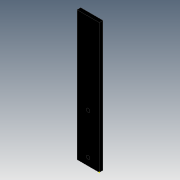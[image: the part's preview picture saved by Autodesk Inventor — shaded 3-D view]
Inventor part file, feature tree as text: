
AUTODESK INVENTOR PART (.ipt)
format: ipt  version: 2015 (Build 190159000, 159)  size: 95,232 bytes
history: native  units: mm
features: other x4, sketch x2, extrude x1, projected_geometry x1
ambient origin geometry x8: Origin, YZ Plane, XZ Plane, XY Plane, X Axis, Y Axis, Z Axis, Center Point
bodies: Body1 (feature_tree)
feature tree (8):
  other  "Blocks"
  extrude  "Extrusion3"  Depth=150.0mm
  sketch  "Sketch3"  dims[d0=60.0mm d1=150.0mm]
  sketch  "Sketch4"  dims[d4=10.0mm d5=10.0mm d6=20.0mm d7=20.0mm d8=30.0mm d11=30.0mm d12=200.0mm d13=10.0mm d14=0.0mm]
  projected_geometry  "Projected Loop1"
  other  "Block1"
  other  "Block1:1"
  other  "Block1:2"
